# Revit family: AUB
name_source: partatom
category: Mechanical Equipment
units: mm (PartAtom-declared; Revit-internal decimal feet)

## family parameters
Always vertical = Yes
Cut with Voids When Loaded = No
Part Type = Normal
Room Calculation Point = No
Round Connector Dimension = Use Diameter
Shared = No
Work Plane-Based = No

## types (5) — shared parameters
0 = 0' - 0"
1" = 0' - 1"
1' = 1' - 0"
1.5 = 0' - 1 1/2"
2" = 0' - 2"
2' = 2' - 0"
4" = 0' - 4"
E = 0' - 3"
E-.125" = 0' - 2 7/8"
Manufacturer = Loren Cook Company
Model = AUB
ONE EIGTH = 0' - 0 1/8"
Type Comments = Propeller Upblast Exhaust Ventilator Aluminum or Steel Roof Mounted/Belt Drive
URL = www.lorencook.com

## per-type parameters (varying)
| type | (A/2)-4" | (A/2)-4.125" | (T_SQ/2)+.125" | -(A/2) | -(C/2) | A | A/2 | B | B/2 | C-B | C-B-3" | C_ | C_/2 | D | E+C-B-2" | RO | RO/2 | T_SQ | T_SQ/2 | T_SQ/6 |
| 24_AUB | 0' - 11 1/2" | 0' - 11 3/8" | 1' - 6 1/8" | -1' - 3 1/2" | -0' - 9 3/4" | 2' - 7" | 1' - 3 1/2" | 1' - 7 1/2" | 0' - 9 3/4" | 2' - 4 1/4" | 2' - 1 1/4" | 3' - 11 3/4" | 1' - 11 7/8" | 0' - 4" | 2' - 5 1/4" | 2' - 7 1/2" | 1' - 3 3/4" | 3' - 0" | 1' - 6" | 0' - 6" |
| 30_AUB | 1' - 2 1/2" | 1' - 2 3/8" | 1' - 9 1/8" | -1' - 6 1/2" | -0' - 11 13/16" | 3' - 1" | 1' - 6 1/2" | 1' - 11 5/8" | 0' - 11 13/16" | 2' - 4 3/4" | 2' - 1 3/4" | 4' - 4 3/8" | 2' - 2 3/16" | 0' - 3 7/8" | 2' - 5 3/4" | 3' - 1 1/2" | 1' - 6 3/4" | 3' - 6" | 1' - 9" | 0' - 7" |
| 36_AUB | 1' - 5 1/2" | 1' - 5 3/8" | 2' - 0 1/8" | -1' - 9 1/2" | -1' - 0 13/16" | 3' - 7" | 1' - 9 1/2" | 2' - 1 5/8" | 1' - 0 13/16" | 2' - 11 1/4" | 2' - 8 1/4" | 5' - 0 7/8" | 2' - 6 7/16" | 0' - 4" | 3' - 0 1/4" | 3' - 7 1/2" | 1' - 9 3/4" | 4' - 0" | 2' - 0" | 0' - 8" |
| 42_AUB | 1' - 8 1/2" | 1' - 8 3/8" | 2' - 3 1/8" | -2' - 0 1/2" | -1' - 1 15/16" | 4' - 1" | 2' - 0 1/2" | 2' - 3 7/8" | 1' - 1 15/16" | 2' - 11 3/4" | 2' - 8 3/4" | 5' - 3 5/8" | 2' - 7 13/16" | 0' - 4" | 3' - 0 3/4" | 4' - 1 1/2" | 2' - 0 3/4" | 4' - 6" | 2' - 3" | 0' - 9" |
| 48_AUB | 1' - 11 1/2" | 1' - 11 3/8" | 2' - 6 1/8" | -2' - 3 1/2" | -1' - 3 5/8" | 4' - 7" | 2' - 3 1/2" | 2' - 7 1/4" | 1' - 3 5/8" | 2' - 11 3/4" | 2' - 8 3/4" | 5' - 7" | 2' - 9 1/2" | 0' - 4" | 3' - 0 3/4" | 4' - 7 1/2" | 2' - 3 3/4" | 5' - 0" | 2' - 6" | 0' - 10" |

## geometry (parser evidence)
native form markers: Sweep x2
no freeform markers — native parametric forms only
